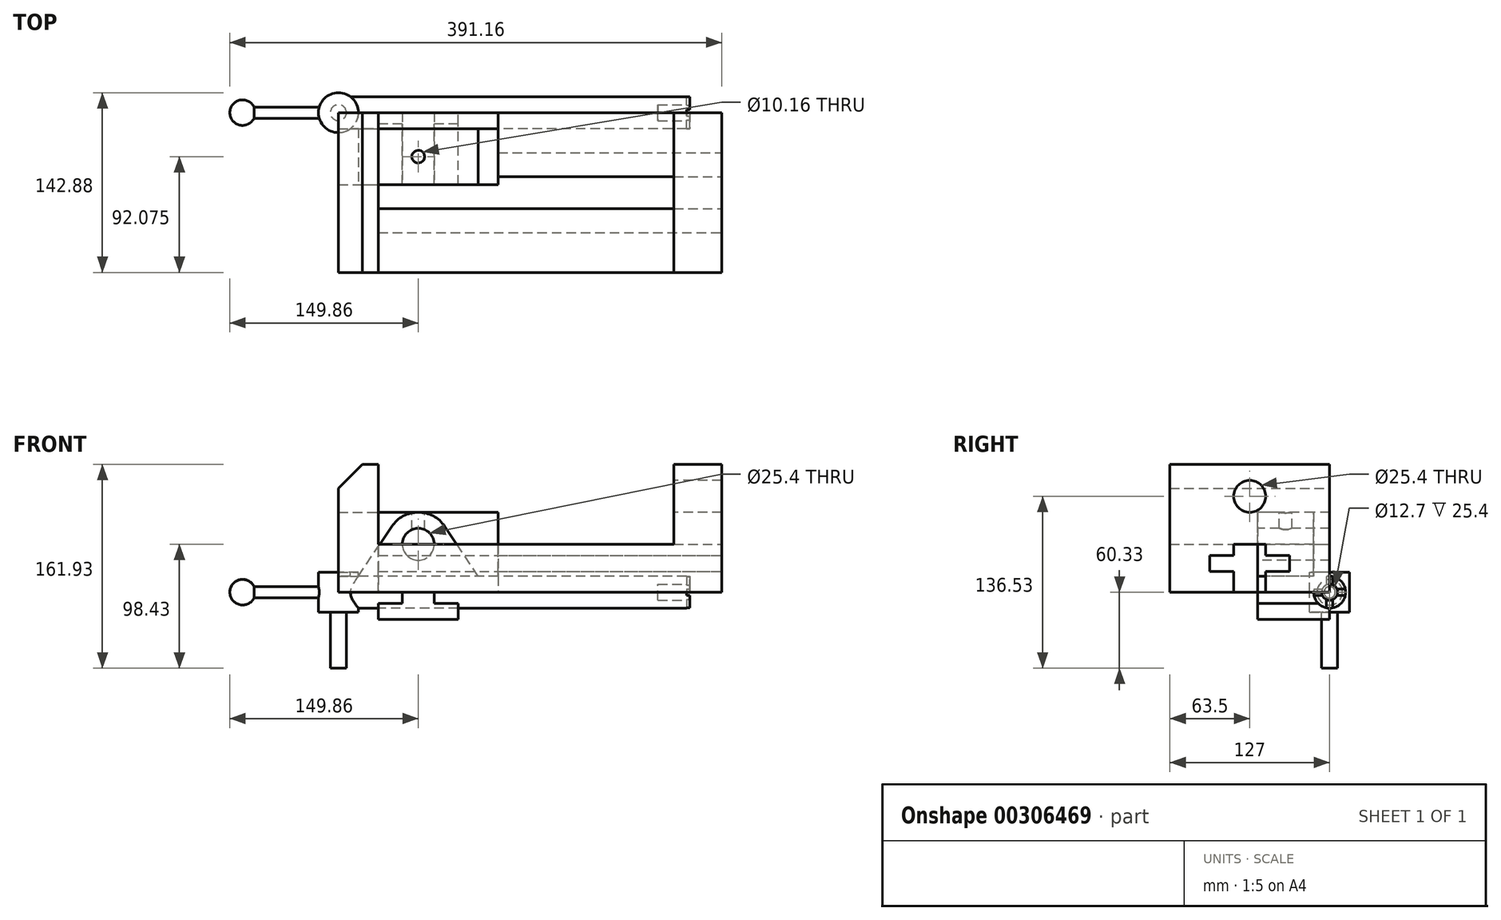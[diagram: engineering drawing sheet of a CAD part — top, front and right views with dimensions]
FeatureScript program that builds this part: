
annotation { "Feature Type Name" : "Feature", "Feature Type Description" : "" }
export const myFeature = defineFeature(function(context is Context, id is Id, definition is map)
    precondition{}
    {
        {
            var Q0;
            Q0=qCreatedBy(makeId("Front.planeOp"),FACE);
            var sketch = newSketch(context, id + "F0", { "sketchPlane" : qUnion([Q0])});
            skLineSegment(sketch, "E0", {"start": v(31.75, 101.6) * mm, "end": v(31.75, 38.1) * mm});
            skLineSegment(sketch, "E1", {"start": v(31.75, 38.1) * mm, "end": v(266.7, 38.1) * mm});
            skLineSegment(sketch, "E2", {"start": v(266.7, 38.1) * mm, "end": v(266.7, 101.6) * mm});
            skLineSegment(sketch, "E3", {"start": v(266.7, 101.6) * mm, "end": v(304.8, 101.6) * mm});
            skLineSegment(sketch, "E4", {"start": v(304.8, 101.6) * mm, "end": v(304.8, 0) * mm});
            skLineSegment(sketch, "E5", {"start": v(304.8, 0) * mm, "end": v(0, 0) * mm});
            skLineSegment(sketch, "E6", {"start": v(0, 0) * mm, "end": v(0, 101.6) * mm});
            skLineSegment(sketch, "E7", {"start": v(0, 101.6) * mm, "end": v(31.75, 101.6) * mm});
            skSolve(sketch);
        }
        {
            var Q0;
            Q0=makeQuery(id+"F0.imprint","IMPRINT",FACE,{"disambiguationData":[TD([[makeQuery(id+"F0.imprint","IMPRINT",EDGE,{"derivedFrom":sQuery(id+"F0.wireOp",EDGE,"E0")}),-1.0]])]});
            extrude(context, id + "F1", {"entities" : qUnion([Q0]), "depth" : 127 * mm});
        }
        {
            var Q0;
            Q0=makeQuery(id+"F1.opExtrude","SWEPT_EDGE",EDGE,{"disambiguationData":[OSD([sQuery(id+"F0.wireOp",EDGE,"E6"),sQuery(id+"F0.wireOp",EDGE,"E7")])]});
            chamfer(context, id + "F2", {"entities" : qUnion([Q0]), "chamferType" : ChamferType.TWO_OFFSETS, "width1" : 19.05 * mm, "oppositeDirection" : false, "width2" : 19.05 * mm, "tangentPropagation" : true});
        }
        {
            var Q0;
            Q0=makeQuery(id+"F1.opExtrude","SWEPT_FACE",FACE,{"disambiguationData":[OSD([sQuery(id+"F0.wireOp",EDGE,"E4")])]});
            var sketch = newSketch(context, id + "F3", { "sketchPlane" : qUnion([Q0])});
            skLineSegment(sketch, "E8", {"start": v(-76.2, 0) * mm, "end": v(-50.8, 0) * mm});
            skLineSegment(sketch, "E9", {"start": v(-50.8, 0) * mm, "end": v(-50.8, 16.51) * mm});
            skLineSegment(sketch, "E10", {"start": v(-50.8, 16.51) * mm, "end": v(-31.75, 16.51) * mm});
            skLineSegment(sketch, "E11", {"start": v(-31.75, 16.51) * mm, "end": v(-31.75, 29.21) * mm});
            skLineSegment(sketch, "E12", {"start": v(-31.75, 29.21) * mm, "end": v(-50.8, 29.21) * mm});
            skLineSegment(sketch, "E13", {"start": v(-50.8, 29.21) * mm, "end": v(-50.8, 38.1) * mm});
            skLineSegment(sketch, "E14", {"start": v(-50.8, 38.1) * mm, "end": v(-76.2, 38.1) * mm});
            skLineSegment(sketch, "E15", {"start": v(-76.2, 38.1) * mm, "end": v(-76.2, 29.21) * mm});
            skLineSegment(sketch, "E16", {"start": v(-76.2, 29.21) * mm, "end": v(-95.25, 29.21) * mm});
            skLineSegment(sketch, "E17", {"start": v(-95.25, 29.21) * mm, "end": v(-95.25, 16.51) * mm});
            skLineSegment(sketch, "E18", {"start": v(-95.25, 16.51) * mm, "end": v(-76.2, 16.51) * mm});
            skLineSegment(sketch, "E19", {"start": v(-76.2, 16.51) * mm, "end": v(-76.2, 0) * mm});
            skLineSegment(sketch, "E20", {"start": v(-63.5, 0) * mm, "end": v(-63.5, 115.04) * mm, "construction": true});
            skSolve(sketch);
        }
        {
            var Q0;
            Q0=makeQuery(id+"F3.imprint","IMPRINT",FACE,{"disambiguationData":[TD([[makeQuery(id+"F3.imprint","IMPRINT",EDGE,{"derivedFrom":sQuery(id+"F3.wireOp",EDGE,"E8")}),1.0]])]});
            var Q1;
            Q1=makeQuery(id+"F1.opExtrude","SWEPT_FACE",FACE,{"disambiguationData":[OSD([sQuery(id+"F0.wireOp",EDGE,"E0")])]});
            extrude(context, id + "F4", {"entities" : qUnion([Q0]), "operationType" : NewBodyOperationType.REMOVE, "endBound" : BoundingType.UP_TO_SURFACE, "oppositeDirection" : true, "endBoundEntityFace" : qUnion([Q1]), "depth" : 25.4 * mm});
        }
        {
            var Q0;
            Q0=makeQuery(id+"F1.opExtrude","SWEPT_FACE",FACE,{"disambiguationData":[OSD([sQuery(id+"F0.wireOp",EDGE,"E2")])]});
            var sketch = newSketch(context, id + "F5", { "sketchPlane" : qUnion([Q0])});
            skLineSegment(sketch, "E21", {"start": v(0, 50.8) * mm, "end": v(127, 50.8) * mm});
            skLineSegment(sketch, "E22", {"start": v(63.5, 101.6) * mm, "end": v(63.5, -10.32) * mm, "construction": true});
            skPoint(sketch, "E22.endSnap0", {"position": v(63.5, 38.1) * mm});
            skCircle(sketch, "E23", {"center": v(63.5, 76.2) * mm, "radius": 12.7 * mm});
            skArc(sketch, "E24", {"start": v(84.6, 90.35) * mm, "mid": v(63.5, 101.6) * mm, "end": v(42.4, 90.35) * mm});
            skLineSegment(sketch, "E25", {"start": v(0, 50.8) * mm, "end": v(15.87, 50.8) * mm});
            skLineSegment(sketch, "E26", {"start": v(127, 50.8) * mm, "end": v(111.12, 50.8) * mm});
            skLineSegment(sketch, "E27", {"start": v(15.87, 50.8) * mm, "end": v(42.4, 90.35) * mm});
            skLineSegment(sketch, "E28", {"start": v(111.13, 50.8) * mm, "end": v(84.6, 90.35) * mm});
            skLineSegment(sketch, "E29", {"start": v(0, 50.8) * mm, "end": v(0, 101.6) * mm});
            skLineSegment(sketch, "E30", {"start": v(0, 101.6) * mm, "end": v(127, 101.6) * mm});
            skLineSegment(sketch, "E31", {"start": v(127, 101.6) * mm, "end": v(127, 50.8) * mm});
            skSolve(sketch);
        }
        {
            var Q0;
            Q0=makeQuery(id+"F5.imprint","IMPRINT",FACE,{"disambiguationData":[TD([[makeQuery(id+"F5.imprint","IMPRINT",EDGE,{"derivedFrom":sQuery(id+"F5.wireOp",EDGE,"E25")}),1.0]])]});
            var Q1;
            Q1=makeQuery(id+"F5.imprint","IMPRINT",FACE,{"disambiguationData":[TD([[makeQuery(id+"F5.imprint","IMPRINT",EDGE,{"derivedFrom":sQuery(id+"F5.wireOp",EDGE,"E26")}),-1.0]])]});
            var Q2;
            Q2=makeQuery(id+"F5.imprint","IMPRINT",FACE,{"disambiguationData":[TD([[makeQuery(id+"F5.imprint","IMPRINT",EDGE,{"derivedFrom":sQuery(id+"F5.wireOp",EDGE,"E23")}),1.0]])]});
            extrude(context, id + "F6", {"entities" : qUnion([Q0, Q1, Q2]), "operationType" : NewBodyOperationType.REMOVE, "endBound" : BoundingType.THROUGH_ALL, "oppositeDirection" : true, "depth" : 25.4 * mm});
        }
        {
            var Q0;
            Q0=qCreatedBy(makeId("Front.planeOp"),FACE);
            var sketch = newSketch(context, id + "F7", { "sketchPlane" : qUnion([Q0])});
            skLineSegment(sketch, "E32", {"start": v(0, 0) * mm, "end": v(0, 63.5) * mm});
            skLineSegment(sketch, "E33", {"start": v(0, 63.5) * mm, "end": v(127, 63.5) * mm});
            skLineSegment(sketch, "E34", {"start": v(127, 63.5) * mm, "end": v(127, 0) * mm});
            skLineSegment(sketch, "E35", {"start": v(127, 0) * mm, "end": v(76.2, 0) * mm});
            skLineSegment(sketch, "E36", {"start": v(76.2, 0) * mm, "end": v(76.2, -8.89) * mm});
            skLineSegment(sketch, "E37", {"start": v(76.2, -8.89) * mm, "end": v(95.25, -8.89) * mm});
            skLineSegment(sketch, "E38", {"start": v(95.25, -8.89) * mm, "end": v(95.25, -21.59) * mm});
            skLineSegment(sketch, "E39", {"start": v(95.25, -21.59) * mm, "end": v(31.75, -21.6) * mm});
            skLineSegment(sketch, "E40", {"start": v(31.75, -21.6) * mm, "end": v(31.75, -8.89) * mm});
            skLineSegment(sketch, "E41", {"start": v(31.75, -8.89) * mm, "end": v(50.8, -8.89) * mm});
            skLineSegment(sketch, "E42", {"start": v(50.8, -8.89) * mm, "end": v(50.8, 0) * mm});
            skLineSegment(sketch, "E43", {"start": v(50.8, 0) * mm, "end": v(0, 0) * mm});
            skLineSegment(sketch, "E44", {"start": v(63.5, 63.5) * mm, "end": v(63.5, -49.06) * mm, "construction": true});
            skSolve(sketch);
        }
        {
            var Q0;
            Q0=makeQuery(id+"F7.imprint","IMPRINT",FACE,{"disambiguationData":[TD([[makeQuery(id+"F7.imprint","IMPRINT",EDGE,{"derivedFrom":sQuery(id+"F7.wireOp",EDGE,"E32")}),-1.0]])]});
            extrude(context, id + "F8", {"entities" : qUnion([Q0]), "depth" : 57.15 * mm});
        }
        {
            var Q0;
            Q0=makeQuery(id+"F8.opExtrude","CAP_FACE",FACE,{"disambiguationData":[OSD([sQuery(id+"F7.wireOp",EDGE,"E32"),sQuery(id+"F7.wireOp",EDGE,"E33"),sQuery(id+"F7.wireOp",EDGE,"E34"),sQuery(id+"F7.wireOp",EDGE,"E35"),sQuery(id+"F7.wireOp",EDGE,"E36"),sQuery(id+"F7.wireOp",EDGE,"E37"),sQuery(id+"F7.wireOp",EDGE,"E38"),sQuery(id+"F7.wireOp",EDGE,"E39"),sQuery(id+"F7.wireOp",EDGE,"E40"),sQuery(id+"F7.wireOp",EDGE,"E41"),sQuery(id+"F7.wireOp",EDGE,"E42"),sQuery(id+"F7.wireOp",EDGE,"E43")])],"isStart":false});
            var sketch = newSketch(context, id + "F9", { "sketchPlane" : qUnion([Q0])});
            skLineSegment(sketch, "E45", {"start": v(0, 0) * mm, "end": v(0, 12.7) * mm});
            skLineSegment(sketch, "E46", {"start": v(127, 0) * mm, "end": v(127, 12.7) * mm});
            skLineSegment(sketch, "E47", {"start": v(63.5, 63.5) * mm, "end": v(63.5, -21.59) * mm, "construction": true});
            skCircle(sketch, "E48", {"center": v(63.5, 38.1) * mm, "radius": 12.7 * mm});
            skArc(sketch, "E49", {"start": v(84.6, 52.25) * mm, "mid": v(63.5, 63.5) * mm, "end": v(42.4, 52.25) * mm});
            skLineSegment(sketch, "E50", {"start": v(0, 12.7) * mm, "end": v(15.88, 12.7) * mm});
            skLineSegment(sketch, "E51", {"start": v(127, 12.7) * mm, "end": v(111.12, 12.7) * mm});
            skLineSegment(sketch, "E52", {"start": v(111.13, 12.7) * mm, "end": v(84.6, 52.25) * mm});
            skLineSegment(sketch, "E53", {"start": v(15.88, 12.7) * mm, "end": v(42.4, 52.25) * mm});
            skLineSegment(sketch, "E54", {"start": v(0, 0) * mm, "end": v(127, 0) * mm});
            skSolve(sketch);
        }
        {
            var Q0;
            {var subQ3=sQuery(id+"F9.wireOp",EDGE,"E50");Q0=makeQuery(id+"F9.imprint","IMPRINT",FACE,{"disambiguationData":[TD([[makeQuery(id+"F9.imprint","IMPRINT",EDGE,{"derivedFrom":subQ3}),1.0]])]});}
            var Q1;
            {var subQ1=sQuery(id+"F9.wireOp",EDGE,"E51");Q1=makeQuery(id+"F9.imprint","IMPRINT",FACE,{"disambiguationData":[TD([[makeQuery(id+"F9.imprint","IMPRINT",EDGE,{"derivedFrom":subQ1}),-1.0]])]});}
            extrude(context, id + "F10", {"entities" : qUnion([Q0, Q1]), "operationType" : NewBodyOperationType.REMOVE, "oppositeDirection" : true, "depth" : 44.45 * mm});
        }
        {
            var Q0;
            Q0=makeQuery(id+"F9.imprint","IMPRINT",FACE,{"disambiguationData":[TD([[makeQuery(id+"F9.imprint","IMPRINT",EDGE,{"derivedFrom":sQuery(id+"F9.wireOp",EDGE,"E48")}),1.0]])]});
            var Q1;
            Q1=sQuery(id+"F9.wireOp",EDGE,"E48");
            extrude(context, id + "F11", {"entities" : qUnion([Q0]), "operationType" : NewBodyOperationType.REMOVE, "surfaceEntities" : qUnion([Q1]), "endBound" : BoundingType.THROUGH_ALL, "oppositeDirection" : true, "depth" : 25.4 * mm});
        }
        {
            var Q0;
            Q0=makeQuery(id+"F8.opExtrude","SWEPT_FACE",FACE,{"disambiguationData":[OSD([sQuery(id+"F7.wireOp",EDGE,"E33")])]});
            var sketch = newSketch(context, id + "F12", { "sketchPlane" : qUnion([Q0])});
            skLineSegment(sketch, "E55", {"start": v(63.5, 0) * mm, "end": v(63.5, -81.82) * mm, "construction": true});
            skCircle(sketch, "E56", {"center": v(63.5, -34.93) * mm, "radius": 5.08 * mm});
            skSolve(sketch);
        }
        {
            var Q0;
            Q0=makeQuery(id+"F12.imprint","IMPRINT",FACE,{"disambiguationData":[TD([[makeQuery(id+"F12.imprint","IMPRINT",EDGE,{"derivedFrom":sQuery(id+"F12.wireOp",EDGE,"E56")}),1.0]])]});
            var Q1;
            Q1=makeQuery(id+"F11.boolean.opBoolean","COPY",FACE,{"derivedFrom":makeQuery(id+"F11.opExtrude","SWEPT_FACE",FACE,{"disambiguationData":[OSD([sQuery(id+"F9.wireOp",EDGE,"E48")])]})});
            extrude(context, id + "F13", {"entities" : qUnion([Q0]), "operationType" : NewBodyOperationType.REMOVE, "endBound" : BoundingType.UP_TO_SURFACE, "oppositeDirection" : true, "endBoundEntityFace" : qUnion([Q1]), "depth" : 25.4 * mm});
        }
        {
            var Q0;
            Q0=qCreatedBy(makeId("Right.planeOp"),FACE);
            var sketch = newSketch(context, id + "F14", { "sketchPlane" : qUnion([Q0])});
            skCircle(sketch, "E57", {"center": v(0, 0) * mm, "radius": 12.7 * mm});
            skSolve(sketch);
        }
        {
            var Q0;
            Q0=makeQuery(id+"F14.imprint","IMPRINT",FACE,{"disambiguationData":[TD([[makeQuery(id+"F14.imprint","IMPRINT",EDGE,{"derivedFrom":sQuery(id+"F14.wireOp",EDGE,"E57")}),1.0]])]});
            extrude(context, id + "F15", {"entities" : qUnion([Q0]), "depth" : 279.4 * mm});
        }
        {
            var Q0;
            Q0=makeQuery(id+"F15.opExtrude","CAP_FACE",FACE,{"disambiguationData":[OSD([sQuery(id+"F14.wireOp",EDGE,"E57")])],"isStart":false});
            var sketch = newSketch(context, id + "F16", { "sketchPlane" : qUnion([Q0])});
            skCircle(sketch, "E58", {"center": v(0, 0) * mm, "radius": 6.35 * mm});
            skCircle(sketch, "E59", {"center": v(0, 0) * mm, "radius": 12.7 * mm});
            skLineSegment(sketch, "E60", {"start": v(-12.44, 2.54) * mm, "end": v(-5.82, 2.54) * mm});
            skLineSegment(sketch, "E61", {"start": v(-12.44, -2.54) * mm, "end": v(-5.82, -2.54) * mm});
            skLineSegment(sketch, "E62", {"start": v(-2.54, 12.44) * mm, "end": v(-2.54, 5.82) * mm});
            skLineSegment(sketch, "E63", {"start": v(2.54, 12.44) * mm, "end": v(2.54, 5.82) * mm});
            skPoint(sketch, "E63.endSnap0", {"position": v(2.54, 2.54) * mm});
            skPoint(sketch, "E64.orphan", {"position": v(-14.45, 2.54) * mm});
            skPoint(sketch, "E65.orphan", {"position": v(2.54, -18.9) * mm});
            skPoint(sketch, "E66.orphan", {"position": v(-2.54, 17.31) * mm});
            skPoint(sketch, "E67.orphan", {"position": v(2.54, 17.31) * mm});
            skPoint(sketch, "E68.orphan", {"position": v(19.53, 2.54) * mm});
            skLineSegment(sketch, "E69.trimOffspring", {"start": v(-2.54, -5.82) * mm, "end": v(-2.54, -12.44) * mm});
            skLineSegment(sketch, "E70.trimOffspring", {"start": v(5.82, 2.54) * mm, "end": v(12.44, 2.54) * mm});
            skLineSegment(sketch, "E71.trimOffspring", {"start": v(2.54, -5.82) * mm, "end": v(2.54, -12.44) * mm});
            skLineSegment(sketch, "E72.trimOffspring", {"start": v(5.82, -2.54) * mm, "end": v(12.44, -2.54) * mm});
            skSolve(sketch);
        }
        {
            var Q0;
            {var subQ0=sQuery(id+"F16.wireOp",EDGE,"E58");var subQ4=makeQuery(id+"F16.imprint","INTERSECT",VERTEX,{"derivedFrom":[subQ0,sQuery(id+"F16.wireOp",EDGE,"E63")]});Q0=makeQuery(id+"F16.imprint","IMPRINT",FACE,{"disambiguationData":[TD([[makeQuery(id+"F16.imprint","IMPRINT",EDGE,{"disambiguationData":[TD([[subQ4,1.0]])],"derivedFrom":subQ0}),1.0]])]});}
            extrude(context, id + "F17", {"entities" : qUnion([Q0]), "operationType" : NewBodyOperationType.REMOVE, "oppositeDirection" : true, "depth" : 25.4 * mm});
        }
        {
            var Q0;
            {var subQ0=sQuery(id+"F16.wireOp",EDGE,"E60");Q0=makeQuery(id+"F16.imprint","IMPRINT",FACE,{"disambiguationData":[TD([[makeQuery(id+"F16.imprint","IMPRINT",EDGE,{"derivedFrom":subQ0}),-1.0]])]});}
            var Q1;
            {var subQ0=sQuery(id+"F16.wireOp",EDGE,"E62");Q1=makeQuery(id+"F16.imprint","IMPRINT",FACE,{"disambiguationData":[TD([[makeQuery(id+"F16.imprint","IMPRINT",EDGE,{"derivedFrom":subQ0}),1.0]])]});}
            var Q2;
            {var subQ0=sQuery(id+"F16.wireOp",EDGE,"E70.trimOffspring");Q2=makeQuery(id+"F16.imprint","IMPRINT",FACE,{"disambiguationData":[TD([[makeQuery(id+"F16.imprint","IMPRINT",EDGE,{"derivedFrom":subQ0}),-1.0]])]});}
            var Q3;
            {var subQ0=sQuery(id+"F16.wireOp",EDGE,"E69.trimOffspring");Q3=makeQuery(id+"F16.imprint","IMPRINT",FACE,{"disambiguationData":[TD([[makeQuery(id+"F16.imprint","IMPRINT",EDGE,{"derivedFrom":subQ0}),1.0]])]});}
            extrude(context, id + "F18", {"entities" : qUnion([Q0, Q1, Q2, Q3]), "operationType" : NewBodyOperationType.REMOVE, "oppositeDirection" : true, "depth" : 2.54 * mm});
        }
        {
            var Q0;
            Q0=qCreatedBy(makeId("Right.planeOp"),FACE);
            var sketch = newSketch(context, id + "F19", { "sketchPlane" : qUnion([Q0])});
            skCircle(sketch, "E73", {"center": v(0, 0) * mm, "radius": 4.45 * mm});
            skSolve(sketch);
        }
        {
            var Q0;
            Q0=makeQuery(id+"F19.imprint","IMPRINT",FACE,{"disambiguationData":[TD([[makeQuery(id+"F19.imprint","IMPRINT",EDGE,{"derivedFrom":sQuery(id+"F19.wireOp",EDGE,"E73")}),1.0]])]});
            extrude(context, id + "F20", {"entities" : qUnion([Q0]), "endBound" : BoundingType.SYMMETRIC, "depth" : 152.4 * mm});
        }
        {
            var Q0;
            Q0=qCreatedBy(makeId("Front.planeOp"),FACE);
            var sketch = newSketch(context, id + "F21", { "sketchPlane" : qUnion([Q0])});
            skLineSegment(sketch, "E74", {"start": v(0, -60.33) * mm, "end": v(6.35, -60.33) * mm});
            skLineSegment(sketch, "E75", {"start": v(6.35, -60.33) * mm, "end": v(6.35, -15.87) * mm});
            skLineSegment(sketch, "E76", {"start": v(6.35, -15.87) * mm, "end": v(15.88, -15.87) * mm});
            skLineSegment(sketch, "E77", {"start": v(15.88, -15.87) * mm, "end": v(15.88, 15.88) * mm});
            skLineSegment(sketch, "E78", {"start": v(15.88, 15.88) * mm, "end": v(0, 15.87) * mm});
            skLineSegment(sketch, "E79", {"start": v(0, 15.88) * mm, "end": v(0, -60.33) * mm});
            skSolve(sketch);
        }
        {
            var Q0;
            Q0=makeQuery(id+"F21.imprint","IMPRINT",FACE,{"disambiguationData":[TD([[makeQuery(id+"F21.imprint","IMPRINT",EDGE,{"derivedFrom":sQuery(id+"F21.wireOp",EDGE,"E74")}),1.0]])]});
            var Q1;
            Q1=sQuery(id+"F21.wireOp",EDGE,"E79");
            revolve(context, id + "F22", {"operationType" : NewBodyOperationType.ADD, "entities" : qUnion([Q0]), "axis" : qUnion([Q1]), "revolveType" : RevolveType.FULL});
        }
        {
            var Q0;
            Q0=qCreatedBy(makeId("Front.planeOp"),FACE);
            var sketch = newSketch(context, id + "F23", { "sketchPlane" : qUnion([Q0])});
            skLineSegment(sketch, "E80", {"start": v(-96.34, 0) * mm, "end": v(107.95, 0) * mm, "construction": true});
            skArc(sketch, "E81", {"start": v(-66.04, 0) * mm, "mid": v(-76.2, 10.16) * mm, "end": v(-86.36, 0) * mm});
            skLineSegment(sketch, "E82", {"start": v(-86.36, 0) * mm, "end": v(-66.04, 0) * mm});
            skArc(sketch, "E83", {"start": v(86.36, 0) * mm, "mid": v(76.2, 10.16) * mm, "end": v(66.04, 0) * mm});
            skLineSegment(sketch, "E84", {"start": v(66.04, 0) * mm, "end": v(86.36, 0) * mm});
            skSolve(sketch);
        }
        {
            var Q0;
            Q0=makeQuery(id+"F23.imprint","IMPRINT",FACE,{"disambiguationData":[TD([[makeQuery(id+"F23.imprint","IMPRINT",EDGE,{"derivedFrom":sQuery(id+"F23.wireOp",EDGE,"E81")}),1.0]])]});
            var Q1;
            Q1=makeQuery(id+"F23.imprint","IMPRINT",FACE,{"disambiguationData":[TD([[makeQuery(id+"F23.imprint","IMPRINT",EDGE,{"derivedFrom":sQuery(id+"F23.wireOp",EDGE,"E83")}),1.0]])]});
            var Q2;
            Q2=sQuery(id+"F23.wireOp",EDGE,"E82");
            revolve(context, id + "F24", {"operationType" : NewBodyOperationType.ADD, "entities" : qUnion([Q0, Q1]), "axis" : qUnion([Q2]), "revolveType" : RevolveType.FULL});
        }
    });
